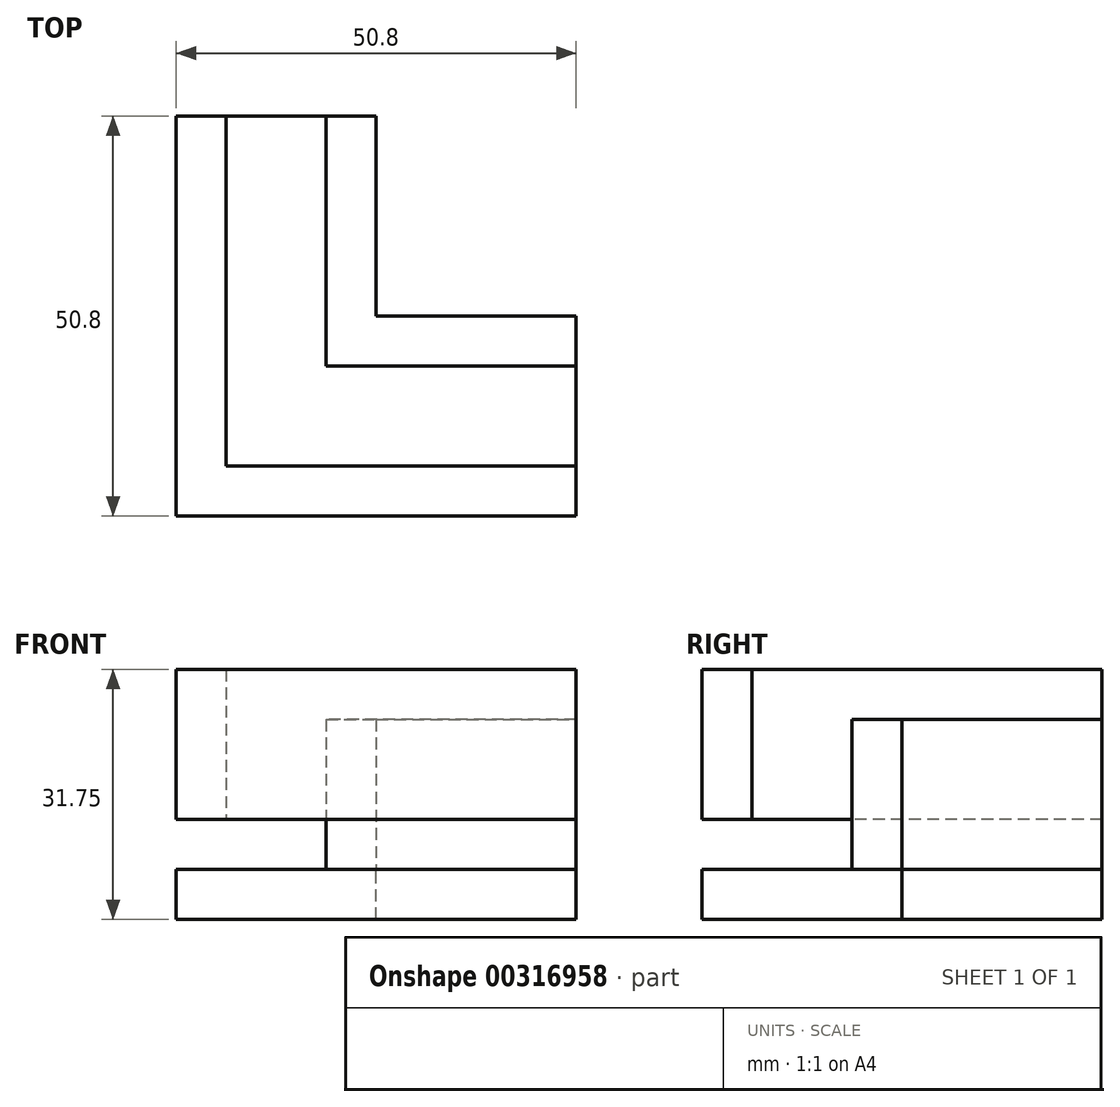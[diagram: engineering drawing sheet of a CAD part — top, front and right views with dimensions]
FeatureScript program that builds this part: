
annotation { "Feature Type Name" : "Feature", "Feature Type Description" : "" }
export const myFeature = defineFeature(function(context is Context, id is Id, definition is map)
    precondition{}
    {
        {
            var Q0;
            Q0=qCreatedBy(makeId("Top.planeOp"),FACE);
            var sketch = newSketch(context, id + "F0", { "sketchPlane" : qUnion([Q0])});
            skLineSegment(sketch, "E0.bottom", {"start": v(25.4, 0) * mm, "end": v(50.8, 0) * mm});
            skLineSegment(sketch, "E0.top", {"start": v(0, -25.4) * mm, "end": v(50.8, -25.4) * mm});
            skLineSegment(sketch, "E0.left", {"start": v(0, 0) * mm, "end": v(0, -25.4) * mm});
            skLineSegment(sketch, "E0.right", {"start": v(50.8, 0) * mm, "end": v(50.8, -25.4) * mm});
            skLineSegment(sketch, "E1.bottom", {"start": v(0, -25.4) * mm, "end": v(25.4, -25.4) * mm});
            skLineSegment(sketch, "E1.top", {"start": v(0, 25.4) * mm, "end": v(6.35, 25.4) * mm});
            skLineSegment(sketch, "E1.left", {"start": v(0, -25.4) * mm, "end": v(0, 25.4) * mm});
            skLineSegment(sketch, "E1.right", {"start": v(25.4, 0) * mm, "end": v(25.4, 25.4) * mm});
            skPoint(sketch, "E2", {"position": v(6.35, 25.4) * mm});
            skPoint(sketch, "E3", {"position": v(19.05, 25.4) * mm});
            skLineSegment(sketch, "E4.trimOffspring", {"start": v(19.05, 25.4) * mm, "end": v(25.4, 25.4) * mm});
            skPoint(sketch, "E5", {"position": v(50.8, -19.05) * mm});
            skPoint(sketch, "E6", {"position": v(50.8, -6.35) * mm});
            skLineSegment(sketch, "E7", {"start": v(50.8, -19.05) * mm, "end": v(6.35, -19.05) * mm});
            skLineSegment(sketch, "E8", {"start": v(50.8, -6.35) * mm, "end": v(19.05, -6.35) * mm});
            skLineSegment(sketch, "E9", {"start": v(6.35, 25.4) * mm, "end": v(6.35, -19.05) * mm});
            skLineSegment(sketch, "E10", {"start": v(19.05, 25.4) * mm, "end": v(19.05, -6.35) * mm});
            skPoint(sketch, "E11.trimOffspring.end.orphan", {"position": v(0, -6.35) * mm});
            skLineSegment(sketch, "E12", {"start": v(6.35, 25.4) * mm, "end": v(19.05, 25.4) * mm});
            skLineSegment(sketch, "E13", {"start": v(50.8, -6.35) * mm, "end": v(50.8, -19.05) * mm});
            skSolve(sketch);
        }
        {
            var Q0;
            {var subQ1=sQuery(id+"F0.wireOp",EDGE,"E0.bottom");Q0=makeQuery(id+"F0.imprint","IMPRINT",FACE,{"disambiguationData":[TD([[makeQuery(id+"F0.imprint","IMPRINT",EDGE,{"derivedFrom":subQ1}),-1.0]])]});}
            var Q1;
            {var subQ3=sQuery(id+"F0.wireOp",EDGE,"E0.top");Q1=makeQuery(id+"F0.imprint","IMPRINT",FACE,{"disambiguationData":[TD([[makeQuery(id+"F0.imprint","IMPRINT",EDGE,{"derivedFrom":subQ3}),1.0]])]});}
            extrude(context, id + "F1", {"entities" : qUnion([Q0, Q1]), "depth" : 19.05 * mm});
        }
        {
            var Q0;
            Q0=makeQuery(id+"F0.imprint","IMPRINT",FACE,{"disambiguationData":[TD([[makeQuery(id+"F0.imprint","IMPRINT",EDGE,{"derivedFrom":sQuery(id+"F0.wireOp",EDGE,"E7")}),-1.0]])]});
            var Q1;
            {var subQ1=sQuery(id+"F0.wireOp",EDGE,"E0.bottom");Q1=makeQuery(id+"F0.imprint","IMPRINT",FACE,{"disambiguationData":[TD([[makeQuery(id+"F0.imprint","IMPRINT",EDGE,{"derivedFrom":subQ1}),-1.0]])]});}
            var Q2;
            {var subQ3=sQuery(id+"F0.wireOp",EDGE,"E0.top");Q2=makeQuery(id+"F0.imprint","IMPRINT",FACE,{"disambiguationData":[TD([[makeQuery(id+"F0.imprint","IMPRINT",EDGE,{"derivedFrom":subQ3}),1.0]])]});}
            extrude(context, id + "F2", {"entities" : qUnion([Q0, Q1, Q2]), "oppositeDirection" : true, "depth" : 6.35 * mm});
        }
        {
            var Q0;
            Q0=makeQuery(id+"F1.opExtrude","SWEPT_BODY",BODY,{"disambiguationData":[OSD([sQuery(id+"F0.wireOp",EDGE,"E0.top"),sQuery(id+"F0.wireOp",EDGE,"E0.right"),sQuery(id+"F0.wireOp",EDGE,"E1.bottom"),sQuery(id+"F0.wireOp",EDGE,"E1.top"),sQuery(id+"F0.wireOp",EDGE,"E1.left"),sQuery(id+"F0.wireOp",EDGE,"E7"),sQuery(id+"F0.wireOp",EDGE,"E9")])]});
            transform(context, id + "F3", {"entities" : qUnion([Q0]), "transformType" : TransformType.TRANSLATION_3D, "dx" : 0 * mm, "dy" : 0 * mm, "dz" : 6.35 * mm, "makeCopy" : false});
        }
    });
